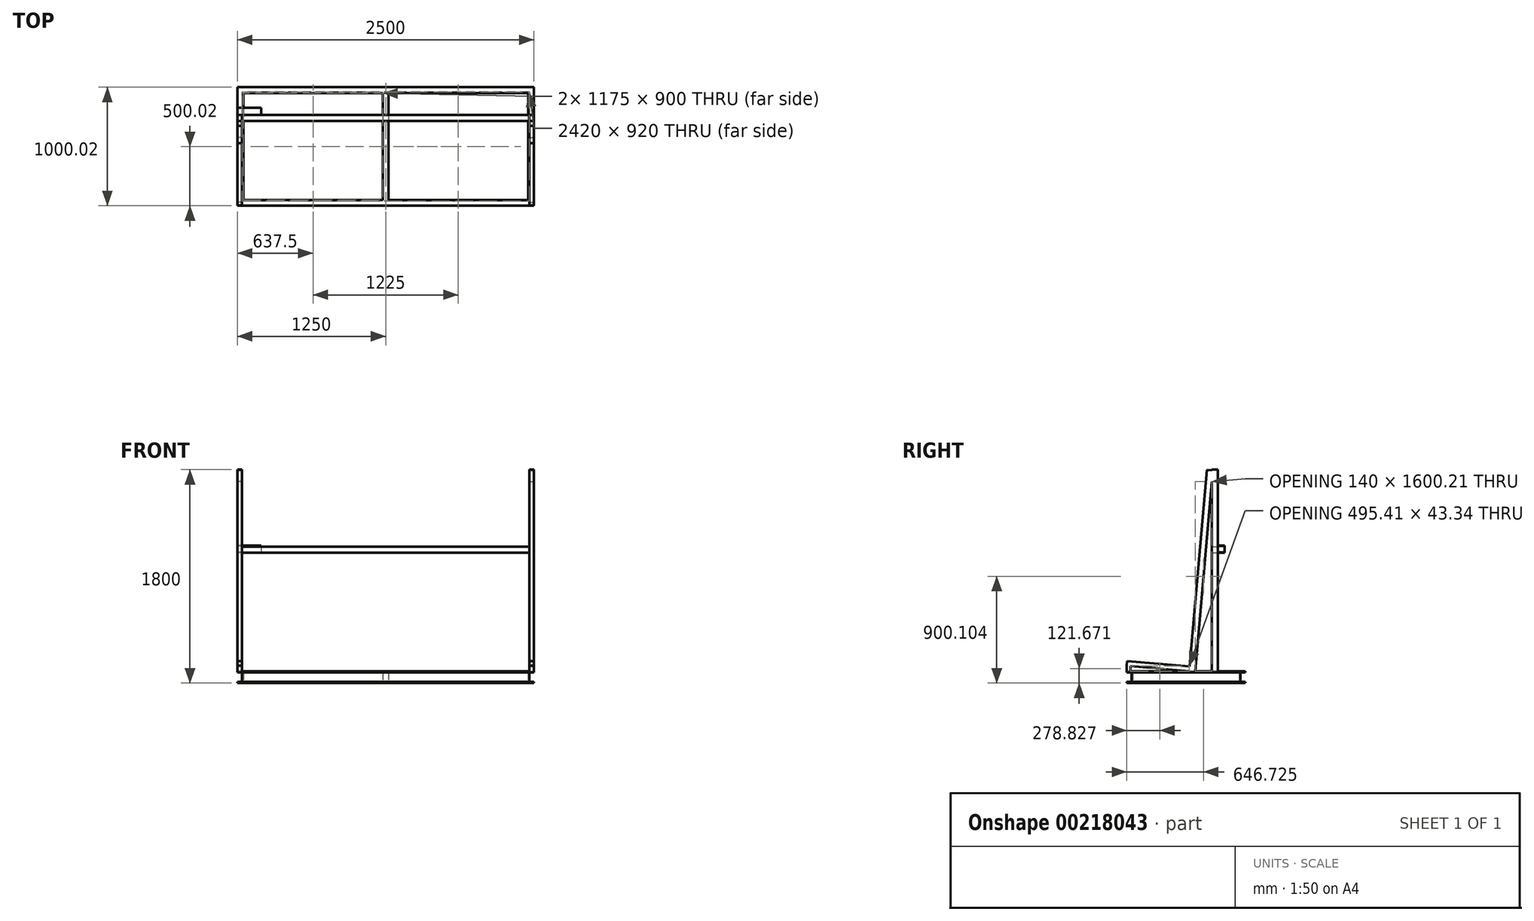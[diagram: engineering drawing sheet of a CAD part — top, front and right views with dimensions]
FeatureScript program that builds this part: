
annotation { "Feature Type Name" : "Feature", "Feature Type Description" : "" }
export const myFeature = defineFeature(function(context is Context, id is Id, definition is map)
    precondition{}
    {
        {
            var Q0;
            Q0=qCreatedBy(makeId("Top.planeOp"),FACE);
            var sketch = newSketch(context, id + "F0", { "sketchPlane" : qUnion([Q0])});
            skLineSegment(sketch, "E0.rect.bottom", {"start": v(1250, 500) * mm, "end": v(-1250, 500) * mm});
            skLineSegment(sketch, "E0.rect.top", {"start": v(1250, -500) * mm, "end": v(-1250, -500) * mm});
            skLineSegment(sketch, "E0.rect.left", {"start": v(1250, 500) * mm, "end": v(1250, -500) * mm});
            skLineSegment(sketch, "E0.rect.right", {"start": v(-1250, 500) * mm, "end": v(-1250, -500) * mm});
            skPoint(sketch, "E0.rect.middle", {"position": v(0, 0) * mm});
            skLineSegment(sketch, "E1.rect.bottom", {"start": v(1200, 450) * mm, "end": v(25, 450) * mm});
            skLineSegment(sketch, "E1.rect.top", {"start": v(1200, -450) * mm, "end": v(25, -450) * mm});
            skLineSegment(sketch, "E1.rect.left", {"start": v(1200, 450) * mm, "end": v(1200, -450) * mm});
            skLineSegment(sketch, "E1.rect.right", {"start": v(-1200, 450) * mm, "end": v(-1200, -450) * mm});
            skLineSegment(sketch, "E2.rect.left", {"start": v(25, 450) * mm, "end": v(25, -450) * mm});
            skLineSegment(sketch, "E2.rect.right", {"start": v(-25, 450) * mm, "end": v(-25, -450) * mm});
            skLineSegment(sketch, "E3.trimOffspring", {"start": v(-25, 450) * mm, "end": v(-1200, 450) * mm});
            skLineSegment(sketch, "E4.trimOffspring", {"start": v(-25, -450) * mm, "end": v(-1200, -450) * mm});
            skSolve(sketch);
        }
        {
            var Q0;
            Q0=makeQuery(id+"F0.imprint","IMPRINT",FACE,{"disambiguationData":[TD([[makeQuery(id+"F0.imprint","IMPRINT",EDGE,{"derivedFrom":sQuery(id+"F0.wireOp",EDGE,"E0.rect.bottom")}),1.0]])]});
            extrude(context, id + "F1", {"entities" : qUnion([Q0]), "depth" : 100 * mm});
        }
        {
            var Q0;
            Q0=makeQuery(id+"F1.opExtrude","SWEPT_FACE",FACE,{"disambiguationData":[OSD([sQuery(id+"F0.wireOp",EDGE,"E0.rect.right")])]});
            var sketch = newSketch(context, id + "F2", { "sketchPlane" : qUnion([Q0])});
            skLineSegment(sketch, "E5.bottom", {"start": v(-500, 90) * mm, "end": v(-460, 90) * mm});
            skLineSegment(sketch, "E5.top", {"start": v(-500, 10) * mm, "end": v(-460, 10) * mm});
            skLineSegment(sketch, "E5.left", {"start": v(-500, 90) * mm, "end": v(-500, 10) * mm});
            skLineSegment(sketch, "E5.right", {"start": v(-460, 90) * mm, "end": v(-460, 10) * mm});
            skLineSegment(sketch, "E6.bottom", {"start": v(500, 90) * mm, "end": v(460, 90) * mm});
            skLineSegment(sketch, "E6.top", {"start": v(500, 10) * mm, "end": v(460, 10) * mm});
            skLineSegment(sketch, "E6.left", {"start": v(500, 90) * mm, "end": v(500, 10) * mm});
            skLineSegment(sketch, "E6.right", {"start": v(460, 90) * mm, "end": v(460, 10) * mm});
            skSolve(sketch);
        }
        {
            var Q0;
            Q0=makeQuery(id+"F2.imprint","IMPRINT",FACE,{"disambiguationData":[TD([[makeQuery(id+"F2.imprint","IMPRINT",EDGE,{"derivedFrom":sQuery(id+"F2.wireOp",EDGE,"E5.bottom")}),-1.0]])]});
            var Q1;
            Q1=makeQuery(id+"F2.imprint","IMPRINT",FACE,{"disambiguationData":[TD([[makeQuery(id+"F2.imprint","IMPRINT",EDGE,{"derivedFrom":sQuery(id+"F2.wireOp",EDGE,"E6.bottom")}),1.0]])]});
            extrude(context, id + "F3", {"entities" : qUnion([Q0, Q1]), "operationType" : NewBodyOperationType.REMOVE, "endBound" : BoundingType.THROUGH_ALL, "oppositeDirection" : true, "depth" : 25 * mm});
        }
        {
            var Q0;
            Q0=makeQuery(id+"F3.boolean.opBoolean","COPY",FACE,{"derivedFrom":makeQuery(id+"F3.opExtrude","SWEPT_FACE",FACE,{"disambiguationData":[OSD([sQuery(id+"F2.wireOp",EDGE,"E6.right")])]})});
            var sketch = newSketch(context, id + "F4", { "sketchPlane" : qUnion([Q0])});
            skLineSegment(sketch, "E7.bottom", {"start": v(1250, 90) * mm, "end": v(1210, 90) * mm});
            skLineSegment(sketch, "E7.top", {"start": v(1250, 10) * mm, "end": v(1210, 10) * mm});
            skLineSegment(sketch, "E7.left", {"start": v(1250, 90) * mm, "end": v(1250, 10) * mm});
            skLineSegment(sketch, "E7.right", {"start": v(1210, 90) * mm, "end": v(1210, 10) * mm});
            skLineSegment(sketch, "E8.bottom", {"start": v(-1250, 90) * mm, "end": v(-1210, 90) * mm});
            skLineSegment(sketch, "E8.top", {"start": v(-1250, 10) * mm, "end": v(-1210, 10) * mm});
            skLineSegment(sketch, "E8.left", {"start": v(-1250, 90) * mm, "end": v(-1250, 10) * mm});
            skLineSegment(sketch, "E8.right", {"start": v(-1210, 90) * mm, "end": v(-1210, 10) * mm});
            skSolve(sketch);
        }
        {
            var Q0;
            Q0=makeQuery(id+"F4.imprint","IMPRINT",FACE,{"disambiguationData":[TD([[makeQuery(id+"F4.imprint","IMPRINT",EDGE,{"derivedFrom":sQuery(id+"F4.wireOp",EDGE,"E7.bottom")}),1.0]])]});
            var Q1;
            Q1=makeQuery(id+"F4.imprint","IMPRINT",FACE,{"disambiguationData":[TD([[makeQuery(id+"F4.imprint","IMPRINT",EDGE,{"derivedFrom":sQuery(id+"F4.wireOp",EDGE,"E8.bottom")}),1.0]])]});
            extrude(context, id + "F5", {"entities" : qUnion([Q0, Q1]), "operationType" : NewBodyOperationType.REMOVE, "endBound" : BoundingType.THROUGH_ALL, "oppositeDirection" : true, "depth" : 25 * mm});
        }
        {
            var Q0;
            Q0=qCreatedBy(makeId("Front.planeOp"),FACE);
            var sketch = newSketch(context, id + "F6", { "sketchPlane" : qUnion([Q0])});
            skLineSegment(sketch, "E9.bottom", {"start": v(0, 10) * mm, "end": v(-90, 10) * mm});
            skLineSegment(sketch, "E9.top", {"start": v(0, 90) * mm, "end": v(-90, 90) * mm});
            skLineSegment(sketch, "E9.left", {"start": v(0, 10) * mm, "end": v(0, 90) * mm});
            skLineSegment(sketch, "E9.right", {"start": v(-90, 10) * mm, "end": v(-90, 90) * mm});
            skSolve(sketch);
        }
        {
            var Q0;
            Q0=qSketchRegion(id+"F6",true);
            var Q1;
            Q1=makeQuery(id+"F1.opExtrude","SWEPT_FACE",FACE,{"disambiguationData":[OSD([sQuery(id+"F0.wireOp",EDGE,"E3.trimOffspring")])]});
            var Q2;
            Q2=makeQuery(id+"F1.opExtrude","SWEPT_FACE",FACE,{"disambiguationData":[OSD([sQuery(id+"F0.wireOp",EDGE,"E4.trimOffspring")])]});
            extrude(context, id + "F7", {"entities" : qUnion([Q0]), "operationType" : NewBodyOperationType.REMOVE, "endBound" : BoundingType.UP_TO_SURFACE, "oppositeDirection" : true, "endBoundEntityFace" : qUnion([Q1]), "depth" : 25 * mm, "hasSecondDirection" : true, "secondDirectionBound" : SecondDirectionBoundingType.UP_TO_SURFACE, "secondDirectionOppositeDirection" : false, "secondDirectionBoundEntityFace" : qUnion([Q2]), "secondDirectionDepth" : 25 * mm});
        }
        {
            var Q0;
            {var subQ1=sQuery(id+"F0.wireOp",EDGE,"E0.rect.right");Q0=makeQuery(id+"FhA0X5EqSXcmZFO_1.boolean.opBoolean","MERGE",FACE,{"derivedFrom":[makeQuery(id+"F5.boolean.opBoolean","SPLIT",FACE,{"disambiguationData":[TD([makeQuery(id+"F3.boolean.opBoolean","COPY",FACE,{"derivedFrom":makeQuery(id+"F3.opExtrude","SWEPT_FACE",FACE,{"disambiguationData":[OSD([sQuery(id+"F2.wireOp",EDGE,"E5.bottom")])]})})])],"derivedFrom":makeQuery(id+"F1.opExtrude","SWEPT_FACE",FACE,{"disambiguationData":[OSD([subQ1])]})}),makeQuery(id+"FhA0X5EqSXcmZFO_1.opExtrude","SWEPT_FACE",FACE,{"disambiguationData":[OSD([sQuery(id+"FkmfJy5WaLFb4fW_1.wireOp",EDGE,"HSkchFZk-3kdc-CD3z-qRNm-T44mPdgp1B9n.left")])]})]});}
            var sketch = newSketch(context, id + "F8", { "sketchPlane" : qUnion([Q0])});
            skLineSegment(sketch, "E10", {"start": v(-76.7, 100) * mm, "end": v(-224.87, 1793.53) * mm});
            skLineSegment(sketch, "E11", {"start": v(-224.87, 1793.53) * mm, "end": v(-175.06, 1797.89) * mm});
            skLineSegment(sketch, "E12", {"start": v(-175.06, 1797.89) * mm, "end": v(-26.51, 100) * mm});
            skLineSegment(sketch, "E13", {"start": v(-26.51, 100) * mm, "end": v(-76.7, 100) * mm});
            skLineSegment(sketch, "E14", {"start": v(-30, 139.85) * mm, "end": v(496.54, 185.91) * mm});
            skLineSegment(sketch, "E15", {"start": v(496.54, 185.91) * mm, "end": v(500.02, 146.07) * mm});
            skLineSegment(sketch, "E16", {"start": v(500.02, 146.07) * mm, "end": v(-26.51, 100) * mm});
            skLineSegment(sketch, "E17", {"start": v(-26.51, 100) * mm, "end": v(-30, 139.85) * mm});
            skLineSegment(sketch, "E18", {"start": v(500, 100) * mm, "end": v(500, 146.06) * mm});
            skLineSegment(sketch, "E19", {"start": v(500, 100) * mm, "end": v(468.9, 100) * mm});
            skLineSegment(sketch, "E20", {"start": v(468.9, 100) * mm, "end": v(468.9, 143.34) * mm});
            skLineSegment(sketch, "E21.top", {"start": v(-266.7, 100) * mm, "end": v(-216.7, 100) * mm});
            skLineSegment(sketch, "E21.right", {"start": v(-216.7, 100) * mm, "end": v(-216.7, 1800) * mm});
            skLineSegment(sketch, "E22.bottom", {"start": v(-266.7, 1800) * mm, "end": v(-216.7, 1800) * mm});
            skLineSegment(sketch, "E22.left", {"start": v(-266.7, 1800) * mm, "end": v(-266.7, 100) * mm});
            skLineSegment(sketch, "E22.right", {"start": v(-216.7, 1800) * mm, "end": v(-216.7, 1800) * mm});
            skSolve(sketch);
        }
        {
            var Q0;
            {var subQ0=sQuery(id+"F8.wireOp",EDGE,"E13");Q0=makeQuery(id+"F8.imprint","IMPRINT",FACE,{"disambiguationData":[TD([[makeQuery(id+"F8.imprint","IMPRINT",EDGE,{"derivedFrom":subQ0}),-1.0]])]});}
            var Q1;
            {var subQ12=sQuery(id+"F8.wireOp",EDGE,"E11");Q1=makeQuery(id+"F8.imprint","IMPRINT",FACE,{"disambiguationData":[TD([[makeQuery(id+"F8.imprint","IMPRINT",EDGE,{"derivedFrom":subQ12}),-1.0]])]});}
            var Q2;
            {var subQ2=sQuery(id+"F8.wireOp",EDGE,"E14");Q2=makeQuery(id+"F8.imprint","IMPRINT",FACE,{"disambiguationData":[TD([[makeQuery(id+"F8.imprint","IMPRINT",EDGE,{"derivedFrom":subQ2}),-1.0]])]});}
            var Q3;
            {var subQ0=sQuery(id+"F8.wireOp",EDGE,"E18");Q3=makeQuery(id+"F8.imprint","IMPRINT",FACE,{"disambiguationData":[TD([[makeQuery(id+"F8.imprint","IMPRINT",EDGE,{"derivedFrom":subQ0}),1.0]])]});}
            var Q4;
            {var subQ0=sQuery(id+"F8.wireOp",EDGE,"E22.top");Q4=makeQuery(id+"F8.imprint","IMPRINT",FACE,{"disambiguationData":[TD([[makeQuery(id+"F8.imprint","IMPRINT",EDGE,{"derivedFrom":subQ0}),1.0]])]});}
            var Q5;
            {var subQ0=sQuery(id+"F8.wireOp",EDGE,"E22.bottom");var subQ3=sQuery(id+"F8.wireOp",EDGE,"E22.right");var subQ5=makeQuery(id+"F8.imprint","INTERSECT",VERTEX,{"derivedFrom":[subQ0,subQ3]});Q5=makeQuery(id+"F8.imprint","IMPRINT",FACE,{"disambiguationData":[TD([[makeQuery(id+"F8.imprint","IMPRINT",EDGE,{"disambiguationData":[TD([[subQ5,-1.0]])],"derivedFrom":subQ3}),-1.0]])]});}
            var Q6;
            {var subQ1=sQuery(id+"F8.wireOp",EDGE,"E12");Q6=makeQuery(id+"F8.imprint","IMPRINT",FACE,{"disambiguationData":[TD([[makeQuery(id+"F8.imprint","IMPRINT",EDGE,{"derivedFrom":subQ1}),-1.0]])]});}
            var Q7;
            {var subQ1=sQuery(id+"F8.wireOp",EDGE,"E21.top");Q7=makeQuery(id+"F8.imprint","IMPRINT",FACE,{"disambiguationData":[TD([[makeQuery(id+"F8.imprint","IMPRINT",EDGE,{"derivedFrom":subQ1}),1.0]])]});}
            extrude(context, id + "F9", {"entities" : qUnion([Q0, Q1, Q2, Q3, Q4, Q5, Q6, Q7]), "operationType" : NewBodyOperationType.ADD, "oppositeDirection" : true, "depth" : 40 * mm});
        }
        {
            var Q0;
            Q0=makeQuery(id+"F9.opExtrude","SWEPT_BODY",BODY,{"disambiguationData":[OSD([sQuery(id+"F8.wireOp",EDGE,"E10"),sQuery(id+"F8.wireOp",EDGE,"E11"),sQuery(id+"F8.wireOp",EDGE,"E12"),sQuery(id+"F8.wireOp",EDGE,"E13")])]});
            var Q1;
            Q1=makeQuery(id+"F1.opExtrude","SWEPT_BODY",BODY,{"disambiguationData":[OSD([sQuery(id+"F0.wireOp",EDGE,"E0.rect.bottom"),sQuery(id+"F0.wireOp",EDGE,"E0.rect.top"),sQuery(id+"F0.wireOp",EDGE,"E0.rect.left"),sQuery(id+"F0.wireOp",EDGE,"E0.rect.right"),sQuery(id+"F0.wireOp",EDGE,"E1.rect.bottom"),sQuery(id+"F0.wireOp",EDGE,"E1.rect.top"),sQuery(id+"F0.wireOp",EDGE,"E1.rect.left"),sQuery(id+"F0.wireOp",EDGE,"E1.rect.right"),sQuery(id+"F0.wireOp",EDGE,"E2.rect.left"),sQuery(id+"F0.wireOp",EDGE,"E2.rect.right"),sQuery(id+"F0.wireOp",EDGE,"E3.trimOffspring"),sQuery(id+"F0.wireOp",EDGE,"E4.trimOffspring")])]});
            var Q2;
            Q2=qCreatedBy(makeId("Right.planeOp"),FACE);
            mirror(context, id + "F10", {"operationType" : NewBodyOperationType.ADD, "entities" : qUnion([Q0, Q1]), "mirrorPlane" : qUnion([Q2])});
        }
        {
            var Q0;
            Q0=makeQuery(id+"F9.opExtrude","CAP_FACE",FACE,{"disambiguationData":[OSD([sQuery(id+"F0.wireOp",EDGE,"E0.rect.right"),sQuery(id+"F8.wireOp",EDGE,"E10"),sQuery(id+"F8.wireOp",EDGE,"E11"),sQuery(id+"F8.wireOp",EDGE,"E12"),sQuery(id+"F8.wireOp",EDGE,"E13"),sQuery(id+"F8.wireOp",EDGE,"E14"),sQuery(id+"F8.wireOp",EDGE,"E15"),sQuery(id+"F8.wireOp",EDGE,"E16"),sQuery(id+"F8.wireOp",EDGE,"E17"),sQuery(id+"F8.wireOp",EDGE,"E18"),sQuery(id+"F8.wireOp",EDGE,"E19"),sQuery(id+"F8.wireOp",EDGE,"E20"),sQuery(id+"F8.wireOp",EDGE,"E22.bottom"),sQuery(id+"F8.wireOp",EDGE,"E22.top"),sQuery(id+"F8.wireOp",EDGE,"E22.left"),sQuery(id+"F8.wireOp",EDGE,"E22.right")])],"isStart":false});
            var sketch = newSketch(context, id + "F11", { "sketchPlane" : qUnion([Q0])});
            skLineSegment(sketch, "E23.bottom", {"start": v(216.7, 1150) * mm, "end": v(266.7, 1150) * mm});
            skLineSegment(sketch, "E23.top", {"start": v(216.7, 1100) * mm, "end": v(266.7, 1100) * mm});
            skLineSegment(sketch, "E23.left", {"start": v(216.7, 1150) * mm, "end": v(216.7, 1100) * mm});
            skLineSegment(sketch, "E23.right", {"start": v(266.7, 1150) * mm, "end": v(266.7, 1100) * mm});
            skSolve(sketch);
        }
        {
            var Q0;
            Q0=makeQuery(id+"F11.imprint","IMPRINT",FACE,{"disambiguationData":[TD([[makeQuery(id+"F11.imprint","IMPRINT",EDGE,{"derivedFrom":sQuery(id+"F11.wireOp",EDGE,"E23.bottom")}),-1.0]])]});
            extrude(context, id + "F12", {"entities" : qUnion([Q0]), "operationType" : NewBodyOperationType.ADD, "endBound" : BoundingType.UP_TO_NEXT, "depth" : 25 * mm});
        }
        {
            var Q0;
            {var subQ0=sQuery(id+"FkmfJy5WaLFb4fW_1.wireOp",EDGE,"HSkchFZk-3kdc-CD3z-qRNm-T44mPdgp1B9n.left");var subQ1=sQuery(id+"F0.wireOp",EDGE,"E0.rect.right");Q0=makeQuery(id+"F9.boolean.opBoolean","MERGE",FACE,{"derivedFrom":[makeQuery(id+"FhA0X5EqSXcmZFO_1.boolean.opBoolean","MERGE",FACE,{"derivedFrom":[makeQuery(id+"F5.boolean.opBoolean","SPLIT",FACE,{"disambiguationData":[TD([makeQuery(id+"F3.boolean.opBoolean","COPY",FACE,{"derivedFrom":makeQuery(id+"F3.opExtrude","SWEPT_FACE",FACE,{"disambiguationData":[OSD([sQuery(id+"F2.wireOp",EDGE,"E5.bottom")])]})})])],"derivedFrom":makeQuery(id+"F1.opExtrude","SWEPT_FACE",FACE,{"disambiguationData":[OSD([subQ1])]})}),makeQuery(id+"FhA0X5EqSXcmZFO_1.opExtrude","SWEPT_FACE",FACE,{"disambiguationData":[OSD([subQ0])]})]}),makeQuery(id+"F9.opExtrude","CAP_FACE",FACE,{"disambiguationData":[OSD([subQ1,sQuery(id+"FkmfJy5WaLFb4fW_1.wireOp",EDGE,"HSkchFZk-3kdc-CD3z-qRNm-T44mPdgp1B9n.top"),subQ0,sQuery(id+"F8.wireOp",EDGE,"E10"),sQuery(id+"F8.wireOp",EDGE,"E11"),sQuery(id+"F8.wireOp",EDGE,"E12"),sQuery(id+"F8.wireOp",EDGE,"E13"),sQuery(id+"F8.wireOp",EDGE,"E14"),sQuery(id+"F8.wireOp",EDGE,"E15"),sQuery(id+"F8.wireOp",EDGE,"E16"),sQuery(id+"F8.wireOp",EDGE,"E17"),sQuery(id+"F8.wireOp",EDGE,"E18"),sQuery(id+"F8.wireOp",EDGE,"E19"),sQuery(id+"F8.wireOp",EDGE,"E20")])],"isStart":true})]});}
            var sketch = newSketch(context, id + "F13", { "sketchPlane" : qUnion([Q0])});
            skLineSegment(sketch, "E24.bottom", {"start": v(-266.7, 1160) * mm, "end": v(-326.7, 1160) * mm});
            skLineSegment(sketch, "E24.top", {"start": v(-266.7, 1100) * mm, "end": v(-326.7, 1100) * mm});
            skLineSegment(sketch, "E24.left", {"start": v(-266.7, 1160) * mm, "end": v(-266.7, 1100) * mm});
            skLineSegment(sketch, "E24.right", {"start": v(-326.7, 1160) * mm, "end": v(-326.7, 1100) * mm});
            skLineSegment(sketch, "E25.bottom", {"start": v(-324.2, 1157.5) * mm, "end": v(-269.2, 1157.5) * mm});
            skLineSegment(sketch, "E25.top", {"start": v(-324.2, 1102.5) * mm, "end": v(-269.2, 1102.5) * mm});
            skLineSegment(sketch, "E25.left", {"start": v(-324.2, 1157.5) * mm, "end": v(-324.2, 1102.5) * mm});
            skLineSegment(sketch, "E25.right", {"start": v(-269.2, 1157.5) * mm, "end": v(-269.2, 1102.5) * mm});
            skSolve(sketch);
        }
        {
            var Q0;
            Q0=makeQuery(id+"F13.imprint","IMPRINT",FACE,{"disambiguationData":[TD([[makeQuery(id+"F13.imprint","IMPRINT",EDGE,{"derivedFrom":sQuery(id+"F13.wireOp",EDGE,"E24.bottom")}),1.0]])]});
            extrude(context, id + "F14", {"entities" : qUnion([Q0]), "operationType" : NewBodyOperationType.ADD, "oppositeDirection" : true, "depth" : 200 * mm});
        }
    });
